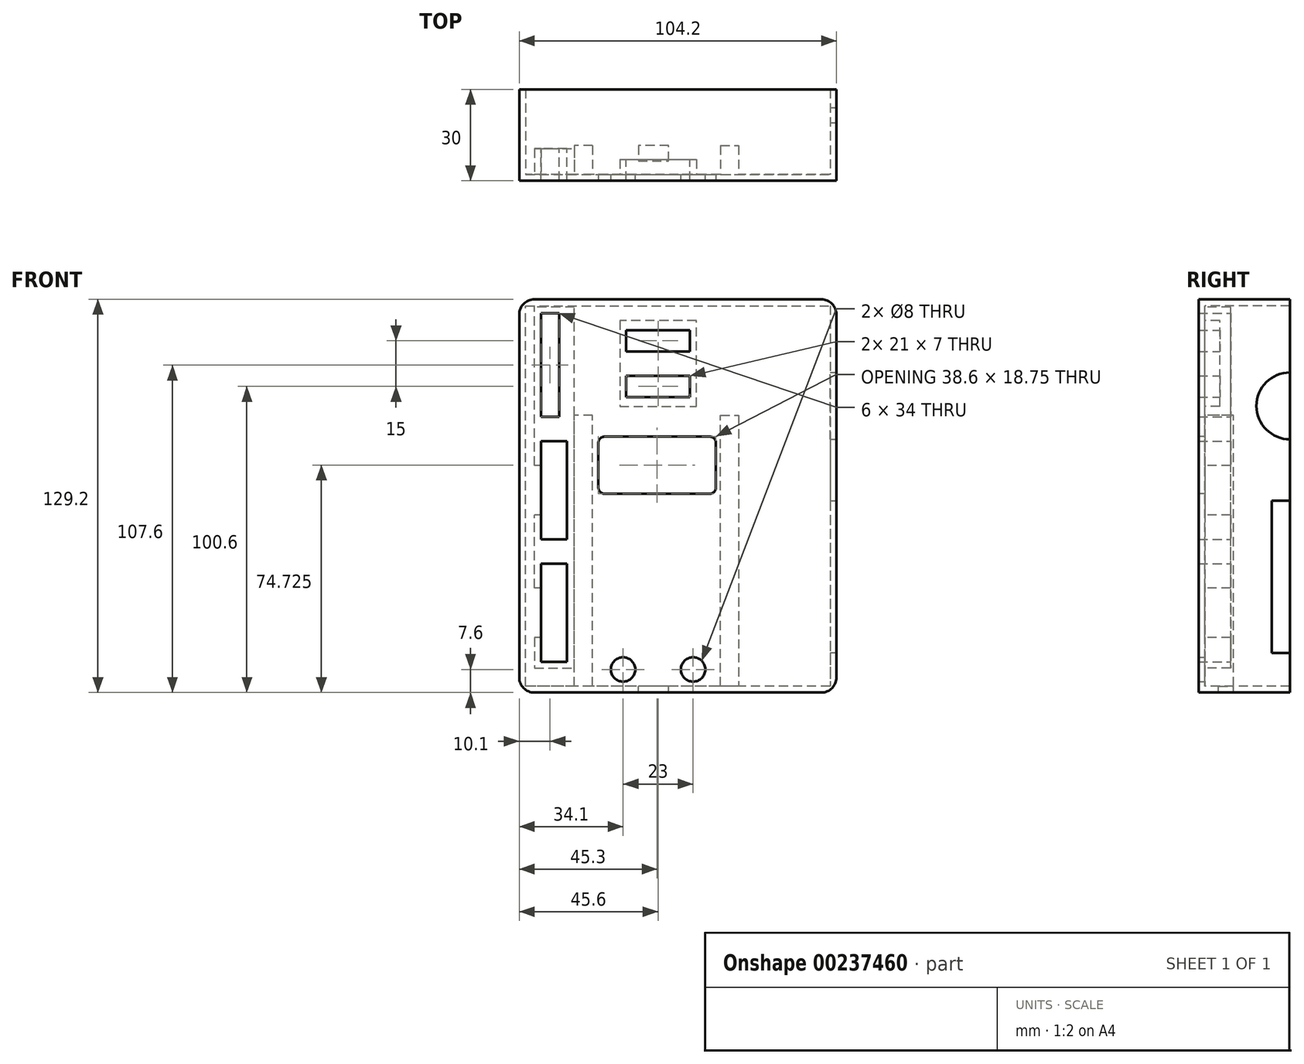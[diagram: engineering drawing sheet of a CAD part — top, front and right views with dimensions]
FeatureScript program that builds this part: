
annotation { "Feature Type Name" : "Feature", "Feature Type Description" : "" }
export const myFeature = defineFeature(function(context is Context, id is Id, definition is map)
    precondition{}
    {
        {
            var Q0;
            Q0=qCreatedBy(makeId("Front.planeOp"),FACE);
            var sketch = newSketch(context, id + "F0", { "sketchPlane" : qUnion([Q0])});
            skLineSegment(sketch, "E0", {"start": v(0, 0) * mm, "end": v(100, 0) * mm});
            skLineSegment(sketch, "E1", {"start": v(100, 0) * mm, "end": v(100, -125) * mm});
            skLineSegment(sketch, "E2", {"start": v(100, -125) * mm, "end": v(0, -125) * mm});
            skLineSegment(sketch, "E3", {"start": v(0, -125) * mm, "end": v(0, 0) * mm});
            skLineSegment(sketch, "E4", {"start": v(0, 0) * mm, "end": v(0, -36) * mm, "construction": true});
            skLineSegment(sketch, "E5", {"start": v(0, -36) * mm, "end": v(16, -36) * mm, "construction": true});
            skLineSegment(sketch, "E6", {"start": v(16, -36) * mm, "end": v(70, -36) * mm, "construction": true});
            skLineSegment(sketch, "E7", {"start": v(16, -36) * mm, "end": v(16, -56) * mm, "construction": true});
            skLineSegment(sketch, "E8", {"start": v(16, -56) * mm, "end": v(34, -56) * mm, "construction": true});
            skLineSegment(sketch, "E9", {"start": v(70, -36) * mm, "end": v(70, -56) * mm, "construction": true});
            skLineSegment(sketch, "E10", {"start": v(70, -56) * mm, "end": v(52, -56) * mm, "construction": true});
            skCircle(sketch, "E11", {"center": v(34, -56) * mm, "radius": 2.75 * mm});
            skCircle(sketch, "E12", {"center": v(52, -56) * mm, "radius": 2.75 * mm});
            skLineSegment(sketch, "E13", {"start": v(70, -36) * mm, "end": v(70, -47) * mm, "construction": true});
            skLineSegment(sketch, "E14", {"start": v(70, -47) * mm, "end": v(58.5, -47) * mm, "construction": true});
            skLineSegment(sketch, "E15", {"start": v(16, -36) * mm, "end": v(16, -47) * mm, "construction": true});
            skLineSegment(sketch, "E16", {"start": v(16, -47) * mm, "end": v(27.5, -47) * mm, "construction": true});
            skCircle(sketch, "E17", {"center": v(27.5, -47) * mm, "radius": 2 * mm});
            skCircle(sketch, "E18", {"center": v(58.5, -47) * mm, "radius": 2 * mm});
            skLineSegment(sketch, "E19", {"start": v(16, -36) * mm, "end": v(16, -41.5) * mm});
            skLineSegment(sketch, "E20", {"start": v(16, -36) * mm, "end": v(16, -125) * mm, "construction": true});
            skLineSegment(sketch, "E21", {"start": v(16, -125) * mm, "end": v(70, -125) * mm, "construction": true});
            skLineSegment(sketch, "E22", {"start": v(70, -125) * mm, "end": v(70, -36) * mm, "construction": true});
            skLineSegment(sketch, "E23", {"start": v(16, -125) * mm, "end": v(16, -119.5) * mm, "construction": true});
            skLineSegment(sketch, "E24", {"start": v(16, -119.5) * mm, "end": v(32, -119.5) * mm, "construction": true});
            skCircle(sketch, "E25", {"center": v(32, -119.5) * mm, "radius": 4 * mm});
            skLineSegment(sketch, "E26", {"start": v(70, -125) * mm, "end": v(70, -119.5) * mm, "construction": true});
            skLineSegment(sketch, "E27", {"start": v(70, -119.5) * mm, "end": v(55, -119.5) * mm, "construction": true});
            skCircle(sketch, "E28", {"center": v(55, -119.5) * mm, "radius": 4 * mm});
            skLineSegment(sketch, "E29", {"start": v(0, -125) * mm, "end": v(0, -117) * mm, "construction": true});
            skLineSegment(sketch, "E30", {"start": v(0, -117) * mm, "end": v(5, -117) * mm, "construction": true});
            skLineSegment(sketch, "E31", {"start": v(5, -117) * mm, "end": v(5, -84.75) * mm});
            skLineSegment(sketch, "E32", {"start": v(5, -84.75) * mm, "end": v(13.5, -84.75) * mm});
            skLineSegment(sketch, "E33", {"start": v(13.5, -84.75) * mm, "end": v(13.5, -117) * mm});
            skLineSegment(sketch, "E34", {"start": v(13.5, -117) * mm, "end": v(5, -117) * mm});
            skLineSegment(sketch, "E35", {"start": v(5, -84.75) * mm, "end": v(5, -76.75) * mm, "construction": true});
            skLineSegment(sketch, "E36", {"start": v(5, -76.75) * mm, "end": v(13.5, -76.75) * mm});
            skLineSegment(sketch, "E37", {"start": v(13.5, -76.75) * mm, "end": v(13.5, -44.5) * mm});
            skLineSegment(sketch, "E38", {"start": v(13.5, -44.5) * mm, "end": v(5, -44.5) * mm});
            skLineSegment(sketch, "E39", {"start": v(5, -44.5) * mm, "end": v(5, -76.75) * mm});
            skLineSegment(sketch, "E40", {"start": v(5, -44.5) * mm, "end": v(5, -36.5) * mm, "construction": true});
            skLineSegment(sketch, "E41", {"start": v(5, -36.5) * mm, "end": v(11, -36.5) * mm});
            skLineSegment(sketch, "E42", {"start": v(11, -36.5) * mm, "end": v(11, -2.5) * mm});
            skLineSegment(sketch, "E43", {"start": v(11, -2.5) * mm, "end": v(5, -2.5) * mm});
            skLineSegment(sketch, "E44", {"start": v(5, -2.5) * mm, "end": v(5, -36.5) * mm});
            skLineSegment(sketch, "E45", {"start": v(0, 0) * mm, "end": v(33, 0) * mm, "construction": true});
            skLineSegment(sketch, "E46", {"start": v(33, 0) * mm, "end": v(33, -8) * mm, "construction": true});
            skLineSegment(sketch, "E47.bottom", {"start": v(33, -8) * mm, "end": v(54, -8) * mm});
            skLineSegment(sketch, "E47.top", {"start": v(33, -15) * mm, "end": v(54, -15) * mm});
            skLineSegment(sketch, "E47.left", {"start": v(33, -8) * mm, "end": v(33, -15) * mm});
            skLineSegment(sketch, "E47.right", {"start": v(54, -8) * mm, "end": v(54, -15) * mm});
            skLineSegment(sketch, "E48", {"start": v(33, -15) * mm, "end": v(33, -23) * mm, "construction": true});
            skLineSegment(sketch, "E49.bottom", {"start": v(33, -23) * mm, "end": v(54, -23) * mm});
            skLineSegment(sketch, "E49.top", {"start": v(33, -30) * mm, "end": v(54, -30) * mm});
            skLineSegment(sketch, "E49.left", {"start": v(33, -23) * mm, "end": v(33, -30) * mm});
            skLineSegment(sketch, "E49.right", {"start": v(54, -23) * mm, "end": v(54, -30) * mm});
            skSolve(sketch);
        }
        {
            var Q0;
            Q0 = qSketchRegion(id + "F0", true);
            extrude(context, id + "F1", {"entities" : qUnion([Q0]), "depth" : 2 * mm});
        }
        {
            var Q0;
            Q0=makeQuery(id+"F1.opExtrude","CAP_FACE",FACE,{"disambiguationData":[OSD([sQuery(id+"F0.wireOp",EDGE,"E0"),sQuery(id+"F0.wireOp",EDGE,"E1"),sQuery(id+"F0.wireOp",EDGE,"E2"),sQuery(id+"F0.wireOp",EDGE,"E3"),sQuery(id+"F0.wireOp",EDGE,"E11"),sQuery(id+"F0.wireOp",EDGE,"E12"),sQuery(id+"F0.wireOp",EDGE,"E17"),sQuery(id+"F0.wireOp",EDGE,"E18"),sQuery(id+"F0.wireOp",EDGE,"E25"),sQuery(id+"F0.wireOp",EDGE,"E28"),sQuery(id+"F0.wireOp",EDGE,"E31"),sQuery(id+"F0.wireOp",EDGE,"E32"),sQuery(id+"F0.wireOp",EDGE,"E33"),sQuery(id+"F0.wireOp",EDGE,"E34"),sQuery(id+"F0.wireOp",EDGE,"E36"),sQuery(id+"F0.wireOp",EDGE,"E37"),sQuery(id+"F0.wireOp",EDGE,"E38"),sQuery(id+"F0.wireOp",EDGE,"E39"),sQuery(id+"F0.wireOp",EDGE,"E41"),sQuery(id+"F0.wireOp",EDGE,"E42"),sQuery(id+"F0.wireOp",EDGE,"E43"),sQuery(id+"F0.wireOp",EDGE,"E44")])],"isStart":true});
            var sketch = newSketch(context, id + "F2", { "sketchPlane" : qUnion([Q0])});
            skLineSegment(sketch, "E50", {"start": v(-13.5, -117) * mm, "end": v(-16, -117) * mm, "construction": true});
            skLineSegment(sketch, "E51", {"start": v(-16, -125) * mm, "end": v(-22, -125) * mm});
            skLineSegment(sketch, "E52", {"start": v(-22, -125) * mm, "end": v(-22, -36) * mm});
            skLineSegment(sketch, "E53", {"start": v(-22, -36) * mm, "end": v(-16, -36) * mm});
            skLineSegment(sketch, "E54", {"start": v(-16, -36) * mm, "end": v(-16, -117) * mm});
            skLineSegment(sketch, "E55", {"start": v(-16, -125) * mm, "end": v(-16, -117) * mm});
            skLineSegment(sketch, "E56", {"start": v(-100, -125) * mm, "end": v(-70, -125) * mm, "construction": true});
            skLineSegment(sketch, "E57", {"start": v(-70, -125) * mm, "end": v(-64, -125) * mm});
            skLineSegment(sketch, "E58", {"start": v(-64, -125) * mm, "end": v(-64, -36) * mm});
            skLineSegment(sketch, "E59", {"start": v(-64, -36) * mm, "end": v(-70, -36) * mm});
            skLineSegment(sketch, "E60", {"start": v(-70, -36) * mm, "end": v(-70, -125) * mm});
            skSolve(sketch);
        }
        {
            var Q0;
            Q0 = qSketchRegion(id + "F2", true);
            extrude(context, id + "F3", {"entities" : qUnion([Q0]), "operationType" : NewBodyOperationType.ADD, "depth" : 8.5 * mm});
        }
        {
            var Q0;
            Q0=makeQuery(id+"F1.opExtrude","CAP_FACE",FACE,{"disambiguationData":[OSD([sQuery(id+"F0.wireOp",EDGE,"E0"),sQuery(id+"F0.wireOp",EDGE,"E1"),sQuery(id+"F0.wireOp",EDGE,"E2"),sQuery(id+"F0.wireOp",EDGE,"E3"),sQuery(id+"F0.wireOp",EDGE,"E11"),sQuery(id+"F0.wireOp",EDGE,"E12"),sQuery(id+"F0.wireOp",EDGE,"E17"),sQuery(id+"F0.wireOp",EDGE,"E18"),sQuery(id+"F0.wireOp",EDGE,"E25"),sQuery(id+"F0.wireOp",EDGE,"E28"),sQuery(id+"F0.wireOp",EDGE,"E31"),sQuery(id+"F0.wireOp",EDGE,"E32"),sQuery(id+"F0.wireOp",EDGE,"E33"),sQuery(id+"F0.wireOp",EDGE,"E34"),sQuery(id+"F0.wireOp",EDGE,"E36"),sQuery(id+"F0.wireOp",EDGE,"E37"),sQuery(id+"F0.wireOp",EDGE,"E38"),sQuery(id+"F0.wireOp",EDGE,"E39"),sQuery(id+"F0.wireOp",EDGE,"E41"),sQuery(id+"F0.wireOp",EDGE,"E42"),sQuery(id+"F0.wireOp",EDGE,"E43"),sQuery(id+"F0.wireOp",EDGE,"E44")])],"isStart":true});
            var sketch = newSketch(context, id + "F4", { "sketchPlane" : qUnion([Q0])});
            skLineSegment(sketch, "E61", {"start": v(-5, -117) * mm, "end": v(-5, -119.1) * mm, "construction": true});
            skLineSegment(sketch, "E62", {"start": v(-5, -119.1) * mm, "end": v(-16, -119.1) * mm});
            skLineSegment(sketch, "E63", {"start": v(-5, -84.75) * mm, "end": v(-5, -82.65) * mm, "construction": true});
            skLineSegment(sketch, "E64", {"start": v(-5, -76.75) * mm, "end": v(-5, -78.85) * mm, "construction": true});
            skLineSegment(sketch, "E65", {"start": v(-5, -82.65) * mm, "end": v(-16, -82.65) * mm});
            skLineSegment(sketch, "E66", {"start": v(-16, -82.65) * mm, "end": v(-16, -119.1) * mm});
            skLineSegment(sketch, "E67", {"start": v(-5, -119.1) * mm, "end": v(-2.9, -119.1) * mm});
            skLineSegment(sketch, "E68", {"start": v(-2.9, -82.65) * mm, "end": v(-5, -82.65) * mm});
            skLineSegment(sketch, "E69", {"start": v(-5, -78.85) * mm, "end": v(-16, -78.85) * mm});
            skLineSegment(sketch, "E70", {"start": v(-5, -44.5) * mm, "end": v(-5, -42.4) * mm, "construction": true});
            skLineSegment(sketch, "E71", {"start": v(-5, -78.85) * mm, "end": v(-2.9, -78.85) * mm});
            skLineSegment(sketch, "E72", {"start": v(-16, -42.4) * mm, "end": v(-16, -78.85) * mm});
            skLineSegment(sketch, "E73", {"start": v(-2.9, -42.4) * mm, "end": v(-16, -42.4) * mm});
            skLineSegment(sketch, "E74", {"start": v(-5, -117) * mm, "end": v(-13.5, -117) * mm});
            skLineSegment(sketch, "E75", {"start": v(-13.5, -117) * mm, "end": v(-13.5, -84.75) * mm});
            skLineSegment(sketch, "E76", {"start": v(-13.5, -84.75) * mm, "end": v(-5, -84.75) * mm});
            skLineSegment(sketch, "E77", {"start": v(-13.5, -76.75) * mm, "end": v(-5, -76.75) * mm});
            skLineSegment(sketch, "E78", {"start": v(-5, -44.5) * mm, "end": v(-13.5, -44.5) * mm});
            skLineSegment(sketch, "E79", {"start": v(-13.5, -44.5) * mm, "end": v(-13.5, -76.75) * mm});
            skLineSegment(sketch, "E80", {"start": v(-5, -44.5) * mm, "end": v(-5, -52.5) * mm});
            skLineSegment(sketch, "E81", {"start": v(-5, -52.5) * mm, "end": v(-2.9, -52.5) * mm});
            skLineSegment(sketch, "E82", {"start": v(-2.9, -52.5) * mm, "end": v(-2.9, -42.4) * mm});
            skLineSegment(sketch, "E83", {"start": v(-5, -76.75) * mm, "end": v(-5, -68.75) * mm});
            skLineSegment(sketch, "E84", {"start": v(-5, -68.75) * mm, "end": v(-2.9, -68.75) * mm});
            skLineSegment(sketch, "E85", {"start": v(-2.9, -68.75) * mm, "end": v(-2.9, -78.85) * mm});
            skLineSegment(sketch, "E86", {"start": v(-5, -84.75) * mm, "end": v(-5, -92.75) * mm});
            skLineSegment(sketch, "E87", {"start": v(-5, -92.75) * mm, "end": v(-2.9, -92.75) * mm});
            skLineSegment(sketch, "E88", {"start": v(-2.9, -92.75) * mm, "end": v(-2.9, -82.65) * mm});
            skLineSegment(sketch, "E89", {"start": v(-5, -117) * mm, "end": v(-5, -109) * mm});
            skLineSegment(sketch, "E90", {"start": v(-5, -109) * mm, "end": v(-2.9, -109) * mm});
            skLineSegment(sketch, "E91", {"start": v(-2.9, -109) * mm, "end": v(-2.9, -119.1) * mm});
            skLineSegment(sketch, "E92", {"start": v(-2.9, -82.65) * mm, "end": v(-2.9, -78.85) * mm});
            skLineSegment(sketch, "E93", {"start": v(-16, -82.65) * mm, "end": v(-16, -78.85) * mm});
            skSolve(sketch);
        }
        {
            var Q0;
            Q0 = qSketchRegion(id + "F4", true);
            extrude(context, id + "F5", {"entities" : qUnion([Q0]), "operationType" : NewBodyOperationType.ADD, "depth" : 8.5 * mm});
        }
        {
            var Q0;
            Q0=makeQuery(id+"F1.opExtrude","CAP_FACE",FACE,{"disambiguationData":[OSD([sQuery(id+"F0.wireOp",EDGE,"E0"),sQuery(id+"F0.wireOp",EDGE,"E1"),sQuery(id+"F0.wireOp",EDGE,"E2"),sQuery(id+"F0.wireOp",EDGE,"E3"),sQuery(id+"F0.wireOp",EDGE,"E11"),sQuery(id+"F0.wireOp",EDGE,"E12"),sQuery(id+"F0.wireOp",EDGE,"E17"),sQuery(id+"F0.wireOp",EDGE,"E18"),sQuery(id+"F0.wireOp",EDGE,"E25"),sQuery(id+"F0.wireOp",EDGE,"E28"),sQuery(id+"F0.wireOp",EDGE,"E31"),sQuery(id+"F0.wireOp",EDGE,"E32"),sQuery(id+"F0.wireOp",EDGE,"E33"),sQuery(id+"F0.wireOp",EDGE,"E34"),sQuery(id+"F0.wireOp",EDGE,"E36"),sQuery(id+"F0.wireOp",EDGE,"E37"),sQuery(id+"F0.wireOp",EDGE,"E38"),sQuery(id+"F0.wireOp",EDGE,"E39"),sQuery(id+"F0.wireOp",EDGE,"E41"),sQuery(id+"F0.wireOp",EDGE,"E42"),sQuery(id+"F0.wireOp",EDGE,"E43"),sQuery(id+"F0.wireOp",EDGE,"E44")])],"isStart":true});
            var sketch = newSketch(context, id + "F6", { "sketchPlane" : qUnion([Q0])});
            skLineSegment(sketch, "E94", {"start": v(-5, -36.5) * mm, "end": v(-5, -38.6) * mm, "construction": true});
            skLineSegment(sketch, "E95", {"start": v(-5, -36.5) * mm, "end": v(-2.9, -36.5) * mm, "construction": true});
            skLineSegment(sketch, "E96", {"start": v(-5, -2.5) * mm, "end": v(-2.9, -2.5) * mm, "construction": true});
            skLineSegment(sketch, "E97", {"start": v(-5, -2.5) * mm, "end": v(-5, -0.4) * mm, "construction": true});
            skLineSegment(sketch, "E98", {"start": v(-5, -38.6) * mm, "end": v(-16, -38.6) * mm});
            skLineSegment(sketch, "E99", {"start": v(-16, -38.6) * mm, "end": v(-16, -0.4) * mm});
            skLineSegment(sketch, "E100", {"start": v(-16, -0.4) * mm, "end": v(-2.9, -0.4) * mm});
            skLineSegment(sketch, "E101", {"start": v(-2.9, -0.4) * mm, "end": v(-2.9, -38.6) * mm});
            skLineSegment(sketch, "E102", {"start": v(-2.9, -38.6) * mm, "end": v(-5, -38.6) * mm});
            skLineSegment(sketch, "E103", {"start": v(-11, -36.5) * mm, "end": v(-5, -36.5) * mm});
            skLineSegment(sketch, "E104", {"start": v(-11, -36.5) * mm, "end": v(-11, -2.5) * mm});
            skLineSegment(sketch, "E105", {"start": v(-11, -2.5) * mm, "end": v(-5, -2.5) * mm});
            skLineSegment(sketch, "E106", {"start": v(-5, -36.5) * mm, "end": v(-5, -2.5) * mm});
            skLineSegment(sketch, "E107", {"start": v(-2.9, -38.6) * mm, "end": v(-2.9, -42.4) * mm});
            skLineSegment(sketch, "E108", {"start": v(-2.9, -42.4) * mm, "end": v(-16, -42.4) * mm});
            skLineSegment(sketch, "E109", {"start": v(-16, -42.4) * mm, "end": v(-16, -38.6) * mm});
            skSolve(sketch);
        }
        {
            var Q0;
            Q0 = qSketchRegion(id + "F6", true);
            extrude(context, id + "F7", {"entities" : qUnion([Q0]), "operationType" : NewBodyOperationType.ADD, "depth" : 8.5 * mm});
        }
        {
            var Q0;
            Q0=makeQuery(id+"F1.opExtrude","CAP_FACE",FACE,{"disambiguationData":[OSD([sQuery(id+"F0.wireOp",EDGE,"E0"),sQuery(id+"F0.wireOp",EDGE,"E1"),sQuery(id+"F0.wireOp",EDGE,"E2"),sQuery(id+"F0.wireOp",EDGE,"E3"),sQuery(id+"F0.wireOp",EDGE,"E11"),sQuery(id+"F0.wireOp",EDGE,"E12"),sQuery(id+"F0.wireOp",EDGE,"E17"),sQuery(id+"F0.wireOp",EDGE,"E18"),sQuery(id+"F0.wireOp",EDGE,"E25"),sQuery(id+"F0.wireOp",EDGE,"E28"),sQuery(id+"F0.wireOp",EDGE,"E31"),sQuery(id+"F0.wireOp",EDGE,"E32"),sQuery(id+"F0.wireOp",EDGE,"E33"),sQuery(id+"F0.wireOp",EDGE,"E34"),sQuery(id+"F0.wireOp",EDGE,"E36"),sQuery(id+"F0.wireOp",EDGE,"E37"),sQuery(id+"F0.wireOp",EDGE,"E38"),sQuery(id+"F0.wireOp",EDGE,"E39"),sQuery(id+"F0.wireOp",EDGE,"E41"),sQuery(id+"F0.wireOp",EDGE,"E42"),sQuery(id+"F0.wireOp",EDGE,"E43"),sQuery(id+"F0.wireOp",EDGE,"E44"),sQuery(id+"F0.wireOp",EDGE,"E47.bottom"),sQuery(id+"F0.wireOp",EDGE,"E47.top"),sQuery(id+"F0.wireOp",EDGE,"E47.left"),sQuery(id+"F0.wireOp",EDGE,"E47.right"),sQuery(id+"F0.wireOp",EDGE,"E49.bottom"),sQuery(id+"F0.wireOp",EDGE,"E49.top"),sQuery(id+"F0.wireOp",EDGE,"E49.left"),sQuery(id+"F0.wireOp",EDGE,"E49.right")])],"isStart":true});
            var sketch = newSketch(context, id + "F8", { "sketchPlane" : qUnion([Q0])});
            skLineSegment(sketch, "E110", {"start": v(-54, -30) * mm, "end": v(-54, -31) * mm, "construction": true});
            skLineSegment(sketch, "E111", {"start": v(-54, -23) * mm, "end": v(-54, -22) * mm, "construction": true});
            skLineSegment(sketch, "E112", {"start": v(-54, -15) * mm, "end": v(-54, -16) * mm, "construction": true});
            skLineSegment(sketch, "E113", {"start": v(-54, -8) * mm, "end": v(-54, -7) * mm, "construction": true});
            skLineSegment(sketch, "E114", {"start": v(-54, -31) * mm, "end": v(-54, -33.1) * mm, "construction": true});
            skLineSegment(sketch, "E115", {"start": v(-54, -31) * mm, "end": v(-56.1, -31) * mm, "construction": true});
            skLineSegment(sketch, "E116", {"start": v(-54, -22) * mm, "end": v(-54, -19.9) * mm, "construction": true});
            skLineSegment(sketch, "E117", {"start": v(-54, -16) * mm, "end": v(-54, -18.1) * mm, "construction": true});
            skLineSegment(sketch, "E118", {"start": v(-54, -16) * mm, "end": v(-56.1, -16) * mm, "construction": true});
            skLineSegment(sketch, "E119", {"start": v(-33, -31) * mm, "end": v(-30.9, -31) * mm, "construction": true});
            skLineSegment(sketch, "E120", {"start": v(-54, -33.1) * mm, "end": v(-56.1, -33.1) * mm});
            skLineSegment(sketch, "E121", {"start": v(-56.1, -33.1) * mm, "end": v(-56.1, -19.9) * mm});
            skLineSegment(sketch, "E122", {"start": v(-56.1, -19.9) * mm, "end": v(-30.9, -19.9) * mm});
            skLineSegment(sketch, "E123", {"start": v(-30.9, -19.9) * mm, "end": v(-30.9, -33.1) * mm});
            skLineSegment(sketch, "E124", {"start": v(-30.9, -33.1) * mm, "end": v(-54, -33.1) * mm});
            skLineSegment(sketch, "E125", {"start": v(-54, -18.1) * mm, "end": v(-56.1, -18.1) * mm});
            skLineSegment(sketch, "E126", {"start": v(-54, -7) * mm, "end": v(-54, -4.9) * mm, "construction": true});
            skLineSegment(sketch, "E127", {"start": v(-56.1, -18.1) * mm, "end": v(-56.1, -4.9) * mm});
            skLineSegment(sketch, "E128", {"start": v(-56.1, -4.9) * mm, "end": v(-30.9, -4.9) * mm});
            skLineSegment(sketch, "E129", {"start": v(-30.9, -4.9) * mm, "end": v(-30.9, -18.1) * mm});
            skLineSegment(sketch, "E130", {"start": v(-30.9, -18.1) * mm, "end": v(-54, -18.1) * mm});
            skLineSegment(sketch, "E131.bottom", {"start": v(-33, -8) * mm, "end": v(-54, -8) * mm});
            skLineSegment(sketch, "E131.top", {"start": v(-33, -15) * mm, "end": v(-54, -15) * mm});
            skLineSegment(sketch, "E131.left", {"start": v(-33, -8) * mm, "end": v(-33, -15) * mm});
            skLineSegment(sketch, "E131.right", {"start": v(-54, -8) * mm, "end": v(-54, -15) * mm});
            skLineSegment(sketch, "E132.bottom", {"start": v(-33, -23) * mm, "end": v(-54, -23) * mm});
            skLineSegment(sketch, "E132.top", {"start": v(-33, -30) * mm, "end": v(-54, -30) * mm});
            skLineSegment(sketch, "E132.left", {"start": v(-33, -23) * mm, "end": v(-33, -30) * mm});
            skLineSegment(sketch, "E132.right", {"start": v(-54, -23) * mm, "end": v(-54, -30) * mm});
            skLineSegment(sketch, "E133", {"start": v(-30.9, -19.9) * mm, "end": v(-30.9, -18.1) * mm});
            skLineSegment(sketch, "E134", {"start": v(-56.1, -19.9) * mm, "end": v(-56.1, -18.1) * mm});
            skSolve(sketch);
        }
        {
            var Q0;
            Q0 = qSketchRegion(id + "F8", true);
            extrude(context, id + "F9", {"entities" : qUnion([Q0]), "operationType" : NewBodyOperationType.ADD, "depth" : 5 * mm});
        }
        {
            var Q0;
            Q0=makeQuery(id+"F1.opExtrude","CAP_FACE",FACE,{"disambiguationData":[OSD([sQuery(id+"F0.wireOp",EDGE,"E0"),sQuery(id+"F0.wireOp",EDGE,"E1"),sQuery(id+"F0.wireOp",EDGE,"E2"),sQuery(id+"F0.wireOp",EDGE,"E3"),sQuery(id+"F0.wireOp",EDGE,"E11"),sQuery(id+"F0.wireOp",EDGE,"E12"),sQuery(id+"F0.wireOp",EDGE,"E17"),sQuery(id+"F0.wireOp",EDGE,"E18"),sQuery(id+"F0.wireOp",EDGE,"E25"),sQuery(id+"F0.wireOp",EDGE,"E28"),sQuery(id+"F0.wireOp",EDGE,"E31"),sQuery(id+"F0.wireOp",EDGE,"E32"),sQuery(id+"F0.wireOp",EDGE,"E33"),sQuery(id+"F0.wireOp",EDGE,"E34"),sQuery(id+"F0.wireOp",EDGE,"E36"),sQuery(id+"F0.wireOp",EDGE,"E37"),sQuery(id+"F0.wireOp",EDGE,"E38"),sQuery(id+"F0.wireOp",EDGE,"E39"),sQuery(id+"F0.wireOp",EDGE,"E41"),sQuery(id+"F0.wireOp",EDGE,"E42"),sQuery(id+"F0.wireOp",EDGE,"E43"),sQuery(id+"F0.wireOp",EDGE,"E44"),sQuery(id+"F0.wireOp",EDGE,"E47.bottom"),sQuery(id+"F0.wireOp",EDGE,"E47.top"),sQuery(id+"F0.wireOp",EDGE,"E47.left"),sQuery(id+"F0.wireOp",EDGE,"E47.right"),sQuery(id+"F0.wireOp",EDGE,"E49.bottom"),sQuery(id+"F0.wireOp",EDGE,"E49.top"),sQuery(id+"F0.wireOp",EDGE,"E49.left"),sQuery(id+"F0.wireOp",EDGE,"E49.right")])],"isStart":false});
            var sketch = newSketch(context, id + "F10", { "sketchPlane" : qUnion([Q0])});
            skLineSegment(sketch, "E135", {"start": v(100, 0) * mm, "end": v(100, 2.1) * mm, "construction": true});
            skLineSegment(sketch, "E136", {"start": v(100, 0) * mm, "end": v(102.1, 0) * mm, "construction": true});
            skLineSegment(sketch, "E137", {"start": v(0, -125) * mm, "end": v(0, -127.1) * mm, "construction": true});
            skLineSegment(sketch, "E138", {"start": v(0, -125) * mm, "end": v(-2.1, -125) * mm, "construction": true});
            skLineSegment(sketch, "E139.bottom", {"start": v(102.1, 2.1) * mm, "end": v(-2.1, 2.1) * mm});
            skLineSegment(sketch, "E139.top", {"start": v(102.1, -127.1) * mm, "end": v(-2.1, -127.1) * mm});
            skLineSegment(sketch, "E139.left", {"start": v(102.1, 2.1) * mm, "end": v(102.1, -127.1) * mm});
            skLineSegment(sketch, "E139.right", {"start": v(-2.1, 2.1) * mm, "end": v(-2.1, -127.1) * mm});
            skLineSegment(sketch, "E140.bottom", {"start": v(100, 0) * mm, "end": v(0, 0) * mm});
            skLineSegment(sketch, "E140.top", {"start": v(100, -125) * mm, "end": v(0, -125) * mm});
            skLineSegment(sketch, "E140.left", {"start": v(100, 0) * mm, "end": v(100, -125) * mm});
            skLineSegment(sketch, "E140.right", {"start": v(0, 0) * mm, "end": v(0, -125) * mm});
            skSolve(sketch);
        }
        {
            var Q0;
            Q0 = qSketchRegion(id + "F10", true);
            extrude(context, id + "F11", {"entities" : qUnion([Q0]), "operationType" : NewBodyOperationType.ADD, "oppositeDirection" : true, "depth" : 30 * mm});
        }
        {
            var Q0;
            Q0=makeQuery(id+"F11.opExtrude","SWEPT_FACE",FACE,{"disambiguationData":[OSD([sQuery(id+"F10.wireOp",EDGE,"E139.left")])]});
            var sketch = newSketch(context, id + "F12", { "sketchPlane" : qUnion([Q0])});
            skLineSegment(sketch, "E141", {"start": v(-2, 2.1) * mm, "end": v(-2, -32.9) * mm, "construction": true});
            skLineSegment(sketch, "E142", {"start": v(-2, -32.9) * mm, "end": v(28, -32.9) * mm, "construction": true});
            skLineSegment(sketch, "E143", {"start": v(-2, -127.1) * mm, "end": v(-2, -114.1) * mm, "construction": true});
            skLineSegment(sketch, "E144", {"start": v(-2, -114.1) * mm, "end": v(22, -114.1) * mm, "construction": true});
            skCircle(sketch, "E145", {"center": v(28, -32.9) * mm, "radius": 11 * mm});
            skLineSegment(sketch, "E146", {"start": v(22, -114.1) * mm, "end": v(22, -64.1) * mm});
            skLineSegment(sketch, "E147", {"start": v(22, -64.1) * mm, "end": v(34, -64.1) * mm});
            skLineSegment(sketch, "E148", {"start": v(34, -64.1) * mm, "end": v(34, -114.1) * mm});
            skLineSegment(sketch, "E149", {"start": v(34, -114.1) * mm, "end": v(22, -114.1) * mm});
            skSolve(sketch);
        }
        {
            var Q0;
            Q0 = qSketchRegion(id + "F12", true);
            extrude(context, id + "F13", {"entities" : qUnion([Q0]), "operationType" : NewBodyOperationType.REMOVE, "oppositeDirection" : true, "depth" : 5 * mm});
        }
        {
            var Q0;
            Q0=makeQuery(id+"F1.opExtrude","CAP_FACE",FACE,{"disambiguationData":[OSD([sQuery(id+"F0.wireOp",EDGE,"E0"),sQuery(id+"F0.wireOp",EDGE,"E1"),sQuery(id+"F0.wireOp",EDGE,"E2"),sQuery(id+"F0.wireOp",EDGE,"E3"),sQuery(id+"F0.wireOp",EDGE,"E11"),sQuery(id+"F0.wireOp",EDGE,"E12"),sQuery(id+"F0.wireOp",EDGE,"E17"),sQuery(id+"F0.wireOp",EDGE,"E18"),sQuery(id+"F0.wireOp",EDGE,"E25"),sQuery(id+"F0.wireOp",EDGE,"E28"),sQuery(id+"F0.wireOp",EDGE,"E31"),sQuery(id+"F0.wireOp",EDGE,"E32"),sQuery(id+"F0.wireOp",EDGE,"E33"),sQuery(id+"F0.wireOp",EDGE,"E34"),sQuery(id+"F0.wireOp",EDGE,"E36"),sQuery(id+"F0.wireOp",EDGE,"E37"),sQuery(id+"F0.wireOp",EDGE,"E38"),sQuery(id+"F0.wireOp",EDGE,"E39"),sQuery(id+"F0.wireOp",EDGE,"E41"),sQuery(id+"F0.wireOp",EDGE,"E42"),sQuery(id+"F0.wireOp",EDGE,"E43"),sQuery(id+"F0.wireOp",EDGE,"E44"),sQuery(id+"F0.wireOp",EDGE,"E47.bottom"),sQuery(id+"F0.wireOp",EDGE,"E47.top"),sQuery(id+"F0.wireOp",EDGE,"E47.left"),sQuery(id+"F0.wireOp",EDGE,"E47.right"),sQuery(id+"F0.wireOp",EDGE,"E49.bottom"),sQuery(id+"F0.wireOp",EDGE,"E49.top"),sQuery(id+"F0.wireOp",EDGE,"E49.left"),sQuery(id+"F0.wireOp",EDGE,"E49.right")])],"isStart":true});
            var sketch = newSketch(context, id + "F14", { "sketchPlane" : qUnion([Q0])});
            skCircle(sketch, "E150", {"center": v(-34, -56) * mm, "radius": 3.75 * mm});
            skCircle(sketch, "E151", {"center": v(-52, -56) * mm, "radius": 3.75 * mm});
            skSolve(sketch);
        }
        {
            var Q0;
            Q0 = qSketchRegion(id + "F14", true);
            extrude(context, id + "F15", {"entities" : qUnion([Q0]), "operationType" : NewBodyOperationType.REMOVE, "oppositeDirection" : true, "depth" : 1 * mm});
        }
        {
            var Q0;
            Q0=makeQuery(id+"F7.boolean.opBoolean","MERGE",FACE,{"derivedFrom":[makeQuery(id+"F5.boolean.opBoolean","MERGE",FACE,{"derivedFrom":[makeQuery(id+"F3.opExtrude","CAP_FACE",FACE,{"disambiguationData":[OSD([sQuery(id+"F2.wireOp",EDGE,"E51"),sQuery(id+"F2.wireOp",EDGE,"E52"),sQuery(id+"F2.wireOp",EDGE,"E53"),sQuery(id+"F2.wireOp",EDGE,"E54"),sQuery(id+"F2.wireOp",EDGE,"E55")])],"isStart":false}),makeQuery(id+"F5.opExtrude","CAP_FACE",FACE,{"disambiguationData":[OSD([sQuery(id+"F4.wireOp",EDGE,"E62"),sQuery(id+"F4.wireOp",EDGE,"E65"),sQuery(id+"F4.wireOp",EDGE,"E66"),sQuery(id+"F4.wireOp",EDGE,"E67"),sQuery(id+"F4.wireOp",EDGE,"E68"),sQuery(id+"F4.wireOp",EDGE,"E74"),sQuery(id+"F4.wireOp",EDGE,"E75"),sQuery(id+"F4.wireOp",EDGE,"E76"),sQuery(id+"F4.wireOp",EDGE,"E86"),sQuery(id+"F4.wireOp",EDGE,"E87"),sQuery(id+"F4.wireOp",EDGE,"E88"),sQuery(id+"F4.wireOp",EDGE,"E89"),sQuery(id+"F4.wireOp",EDGE,"E90"),sQuery(id+"F4.wireOp",EDGE,"E91")])],"isStart":false}),makeQuery(id+"F5.opExtrude","CAP_FACE",FACE,{"disambiguationData":[OSD([sQuery(id+"F4.wireOp",EDGE,"E69"),sQuery(id+"F4.wireOp",EDGE,"E71"),sQuery(id+"F4.wireOp",EDGE,"E72"),sQuery(id+"F4.wireOp",EDGE,"E73"),sQuery(id+"F4.wireOp",EDGE,"E77"),sQuery(id+"F4.wireOp",EDGE,"E78"),sQuery(id+"F4.wireOp",EDGE,"E79"),sQuery(id+"F4.wireOp",EDGE,"E80"),sQuery(id+"F4.wireOp",EDGE,"E81"),sQuery(id+"F4.wireOp",EDGE,"E82"),sQuery(id+"F4.wireOp",EDGE,"E83"),sQuery(id+"F4.wireOp",EDGE,"E84"),sQuery(id+"F4.wireOp",EDGE,"E85")])],"isStart":false})]}),makeQuery(id+"F7.opExtrude","CAP_FACE",FACE,{"disambiguationData":[OSD([sQuery(id+"F6.wireOp",EDGE,"E98"),sQuery(id+"F6.wireOp",EDGE,"E99"),sQuery(id+"F6.wireOp",EDGE,"E100"),sQuery(id+"F6.wireOp",EDGE,"E101"),sQuery(id+"F6.wireOp",EDGE,"E102"),sQuery(id+"F6.wireOp",EDGE,"E103"),sQuery(id+"F6.wireOp",EDGE,"E104"),sQuery(id+"F6.wireOp",EDGE,"E105"),sQuery(id+"F6.wireOp",EDGE,"E106")])],"isStart":false})]});
            var sketch = newSketch(context, id + "F16", { "sketchPlane" : qUnion([Q0])});
            skLineSegment(sketch, "E152.bottom", {"start": v(-16, -125) * mm, "end": v(-22, -125) * mm});
            skLineSegment(sketch, "E152.top", {"start": v(-16, -36) * mm, "end": v(-22, -36) * mm});
            skLineSegment(sketch, "E152.left", {"start": v(-16, -125) * mm, "end": v(-16, -36) * mm});
            skLineSegment(sketch, "E152.right", {"start": v(-22, -125) * mm, "end": v(-22, -36) * mm});
            skSolve(sketch);
        }
        {
            var Q0;
            Q0 = qSketchRegion(id + "F16", true);
            extrude(context, id + "F17", {"entities" : qUnion([Q0]), "operationType" : NewBodyOperationType.ADD, "depth" : 1 * mm});
        }
        {
            var Q0;
            Q0=makeQuery(id+"F3.opExtrude","CAP_FACE",FACE,{"disambiguationData":[OSD([sQuery(id+"F2.wireOp",EDGE,"E57"),sQuery(id+"F2.wireOp",EDGE,"E58"),sQuery(id+"F2.wireOp",EDGE,"E59"),sQuery(id+"F2.wireOp",EDGE,"E60")])],"isStart":false});
            var sketch = newSketch(context, id + "F18", { "sketchPlane" : qUnion([Q0])});
            skLineSegment(sketch, "E153.bottom", {"start": v(-64, -125) * mm, "end": v(-70, -125) * mm});
            skLineSegment(sketch, "E153.top", {"start": v(-64, -36) * mm, "end": v(-70, -36) * mm});
            skLineSegment(sketch, "E153.left", {"start": v(-64, -125) * mm, "end": v(-64, -36) * mm});
            skLineSegment(sketch, "E153.right", {"start": v(-70, -125) * mm, "end": v(-70, -36) * mm});
            skSolve(sketch);
        }
        {
            var Q0;
            Q0 = qSketchRegion(id + "F18", true);
            extrude(context, id + "F19", {"entities" : qUnion([Q0]), "operationType" : NewBodyOperationType.ADD, "depth" : 1 * mm});
        }
        {
            var Q0;
            Q0=makeQuery(id+"F11.opExtrude","SWEPT_FACE",FACE,{"disambiguationData":[OSD([sQuery(id+"F10.wireOp",EDGE,"E140.top")])]});
            var sketch = newSketch(context, id + "F20", { "sketchPlane" : qUnion([Q0])});
            skLineSegment(sketch, "E154", {"start": v(16, 9.5) * mm, "end": v(37, 9.5) * mm, "construction": true});
            skLineSegment(sketch, "E155", {"start": v(37, 9.5) * mm, "end": v(37, 4.5) * mm});
            skLineSegment(sketch, "E156", {"start": v(37, 4.5) * mm, "end": v(47, 4.5) * mm});
            skLineSegment(sketch, "E157", {"start": v(47, 4.5) * mm, "end": v(47, 9.5) * mm});
            skLineSegment(sketch, "E158", {"start": v(47, 9.5) * mm, "end": v(37, 9.5) * mm});
            skSolve(sketch);
        }
        {
            var Q0;
            Q0 = qSketchRegion(id + "F20", true);
            extrude(context, id + "F21", {"entities" : qUnion([Q0]), "operationType" : NewBodyOperationType.REMOVE, "oppositeDirection" : true, "depth" : 5 * mm});
        }
        {
            var Q0;
            Q0=makeQuery(id+"F11.opExtrude","SWEPT_EDGE",EDGE,{"disambiguationData":[OSD([sQuery(id+"F10.wireOp",EDGE,"E139.bottom"),sQuery(id+"F10.wireOp",EDGE,"E139.left")])]});
            var Q1;
            Q1=makeQuery(id+"F11.opExtrude","SWEPT_EDGE",EDGE,{"disambiguationData":[OSD([sQuery(id+"F10.wireOp",EDGE,"E139.bottom"),sQuery(id+"F10.wireOp",EDGE,"E139.right")])]});
            var Q2;
            Q2=makeQuery(id+"F11.opExtrude","SWEPT_EDGE",EDGE,{"disambiguationData":[OSD([sQuery(id+"F10.wireOp",EDGE,"E139.top"),sQuery(id+"F10.wireOp",EDGE,"E139.right")])]});
            var Q3;
            Q3=makeQuery(id+"F11.opExtrude","SWEPT_EDGE",EDGE,{"disambiguationData":[OSD([sQuery(id+"F10.wireOp",EDGE,"E139.top"),sQuery(id+"F10.wireOp",EDGE,"E139.left")])]});
            fillet(context, id + "F22", {"entities" : qUnion([Q0, Q1, Q2, Q3]), "radius" : 5 * mm, "tangentPropagation" : true, "allowEdgeOverflow" : false});
        }
        {
            var Q0;
            Q0=makeQuery(id+"F11.boolean.opBoolean","MERGE",FACE,{"derivedFrom":[makeQuery(id+"F1.opExtrude","CAP_FACE",FACE,{"disambiguationData":[OSD([sQuery(id+"F0.wireOp",EDGE,"E0"),sQuery(id+"F0.wireOp",EDGE,"E1"),sQuery(id+"F0.wireOp",EDGE,"E2"),sQuery(id+"F0.wireOp",EDGE,"E3"),sQuery(id+"F0.wireOp",EDGE,"E11"),sQuery(id+"F0.wireOp",EDGE,"E12"),sQuery(id+"F0.wireOp",EDGE,"E17"),sQuery(id+"F0.wireOp",EDGE,"E18"),sQuery(id+"F0.wireOp",EDGE,"E25"),sQuery(id+"F0.wireOp",EDGE,"E28"),sQuery(id+"F0.wireOp",EDGE,"E31"),sQuery(id+"F0.wireOp",EDGE,"E32"),sQuery(id+"F0.wireOp",EDGE,"E33"),sQuery(id+"F0.wireOp",EDGE,"E34"),sQuery(id+"F0.wireOp",EDGE,"E36"),sQuery(id+"F0.wireOp",EDGE,"E37"),sQuery(id+"F0.wireOp",EDGE,"E38"),sQuery(id+"F0.wireOp",EDGE,"E39"),sQuery(id+"F0.wireOp",EDGE,"E41"),sQuery(id+"F0.wireOp",EDGE,"E42"),sQuery(id+"F0.wireOp",EDGE,"E43"),sQuery(id+"F0.wireOp",EDGE,"E44"),sQuery(id+"F0.wireOp",EDGE,"E47.bottom"),sQuery(id+"F0.wireOp",EDGE,"E47.top"),sQuery(id+"F0.wireOp",EDGE,"E47.left"),sQuery(id+"F0.wireOp",EDGE,"E47.right"),sQuery(id+"F0.wireOp",EDGE,"E49.bottom"),sQuery(id+"F0.wireOp",EDGE,"E49.top"),sQuery(id+"F0.wireOp",EDGE,"E49.left"),sQuery(id+"F0.wireOp",EDGE,"E49.right")])],"isStart":false}),makeQuery(id+"F11.opExtrude","CAP_FACE",FACE,{"disambiguationData":[OSD([sQuery(id+"F10.wireOp",EDGE,"E139.bottom"),sQuery(id+"F10.wireOp",EDGE,"E139.top"),sQuery(id+"F10.wireOp",EDGE,"E139.left"),sQuery(id+"F10.wireOp",EDGE,"E139.right"),sQuery(id+"F10.wireOp",EDGE,"E140.bottom"),sQuery(id+"F10.wireOp",EDGE,"E140.top"),sQuery(id+"F10.wireOp",EDGE,"E140.left"),sQuery(id+"F10.wireOp",EDGE,"E140.right")])],"isStart":true})]});
            var sketch = newSketch(context, id + "F23", { "sketchPlane" : qUnion([Q0])});
            skLineSegment(sketch, "E159.bottom", {"start": v(23.9, -43) * mm, "end": v(62.5, -43) * mm});
            skLineSegment(sketch, "E159.top", {"start": v(23.9, -61.75) * mm, "end": v(62.5, -61.75) * mm});
            skLineSegment(sketch, "E159.left", {"start": v(23.9, -43) * mm, "end": v(23.9, -61.75) * mm});
            skLineSegment(sketch, "E159.right", {"start": v(62.5, -43) * mm, "end": v(62.5, -61.75) * mm});
            skSolve(sketch);
        }
        {
            var Q0;
            Q0=makeQuery(id+"F23.imprint","IMPRINT",FACE,{"disambiguationData":[TD([[makeQuery(id+"F23.imprint","IMPRINT",EDGE,{"derivedFrom":sQuery(id+"F23.wireOp",EDGE,"E159.bottom")}),-1.0]])]});
            extrude(context, id + "F24", {"entities" : qUnion([Q0]), "operationType" : NewBodyOperationType.REMOVE, "oppositeDirection" : true, "depth" : 25 * mm});
        }
        {
            var Q0;
            Q0=makeQuery(id+"F24.boolean.opBoolean","COPY",EDGE,{"derivedFrom":makeQuery(id+"F24.opExtrude","SWEPT_EDGE",EDGE,{"disambiguationData":[OSD([sQuery(id+"F23.wireOp",EDGE,"E159.bottom"),sQuery(id+"F23.wireOp",EDGE,"E159.left")])]})});
            var Q1;
            Q1=makeQuery(id+"F24.boolean.opBoolean","COPY",EDGE,{"derivedFrom":makeQuery(id+"F24.opExtrude","SWEPT_EDGE",EDGE,{"disambiguationData":[OSD([sQuery(id+"F23.wireOp",EDGE,"E159.bottom"),sQuery(id+"F23.wireOp",EDGE,"E159.right")])]})});
            var Q2;
            Q2=makeQuery(id+"F24.boolean.opBoolean","COPY",EDGE,{"derivedFrom":makeQuery(id+"F24.opExtrude","SWEPT_EDGE",EDGE,{"disambiguationData":[OSD([sQuery(id+"F23.wireOp",EDGE,"E159.top"),sQuery(id+"F23.wireOp",EDGE,"E159.left")])]})});
            var Q3;
            Q3=makeQuery(id+"F24.boolean.opBoolean","COPY",EDGE,{"derivedFrom":makeQuery(id+"F24.opExtrude","SWEPT_EDGE",EDGE,{"disambiguationData":[OSD([sQuery(id+"F23.wireOp",EDGE,"E159.top"),sQuery(id+"F23.wireOp",EDGE,"E159.right")])]})});
            fillet(context, id + "F25", {"entities" : qUnion([Q0, Q1, Q2, Q3]), "radius" : 2 * mm, "tangentPropagation" : true, "allowEdgeOverflow" : false});
        }
    });
